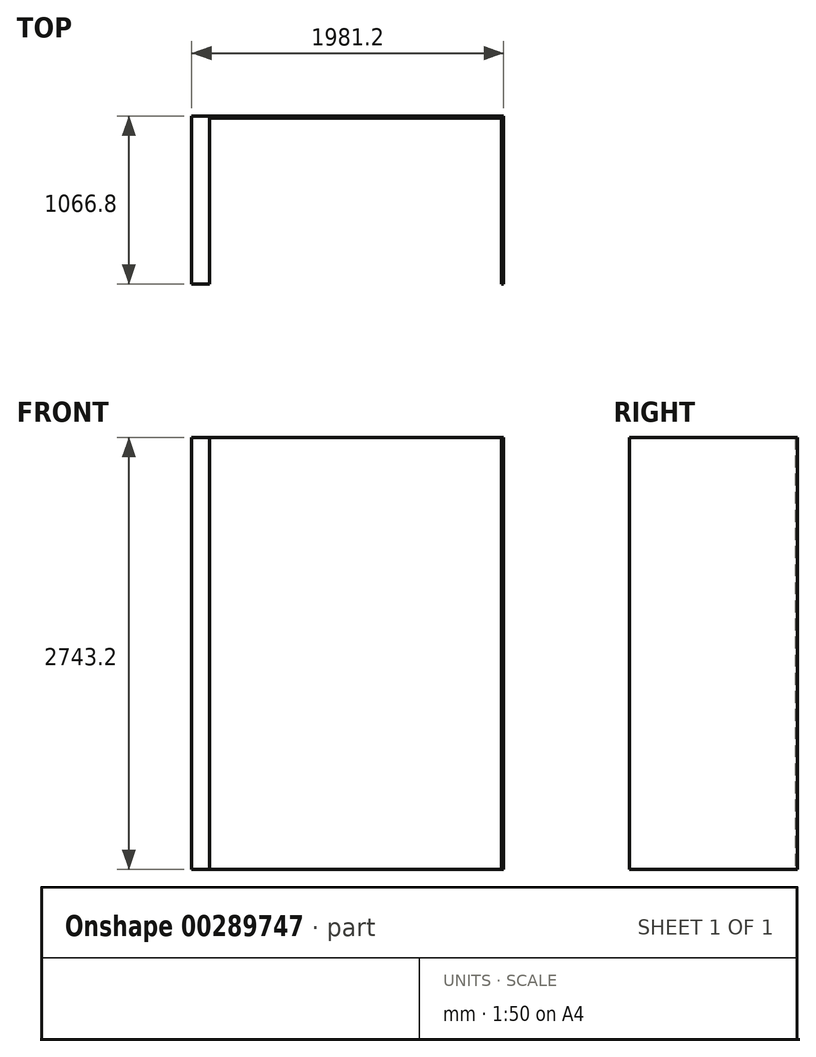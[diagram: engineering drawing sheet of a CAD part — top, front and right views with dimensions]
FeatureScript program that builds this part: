
annotation { "Feature Type Name" : "Feature", "Feature Type Description" : "" }
export const myFeature = defineFeature(function(context is Context, id is Id, definition is map)
    precondition{}
    {
        {
            var Q0;
            Q0=qCreatedBy(makeId("Top.planeOp"),FACE);
            var sketch = newSketch(context, id + "F0", { "sketchPlane" : qUnion([Q0])});
            skLineSegment(sketch, "E0.bottom", {"start": v(990.6, -533.4) * mm, "end": v(-990.6, -533.4) * mm});
            skLineSegment(sketch, "E0.top", {"start": v(990.6, 533.4) * mm, "end": v(-990.6, 533.4) * mm});
            skLineSegment(sketch, "E0.left", {"start": v(990.6, -533.4) * mm, "end": v(990.6, 533.4) * mm});
            skLineSegment(sketch, "E0.right", {"start": v(-990.6, -533.4) * mm, "end": v(-990.6, 533.4) * mm});
            skPoint(sketch, "E0.middle", {"position": v(0, 0) * mm});
            skLineSegment(sketch, "E1", {"start": v(-876.3, -533.4) * mm, "end": v(-876.3, 520.7) * mm});
            skLineSegment(sketch, "E2", {"start": v(-876.3, 520.7) * mm, "end": v(977.9, 520.7) * mm});
            skLineSegment(sketch, "E3", {"start": v(977.9, 520.7) * mm, "end": v(977.9, -533.4) * mm});
            skLineSegment(sketch, "E4", {"start": v(977.9, -533.4) * mm, "end": v(990.6, -533.4) * mm});
            skSolve(sketch);
        }
        {
            var Q0;
            Q0=makeQuery(id+"F0.imprint","IMPRINT",FACE,{"disambiguationData":[TD([[makeQuery(id+"F0.imprint","IMPRINT",EDGE,{"derivedFrom":sQuery(id+"F0.wireOp",EDGE,"E0.top")}),1.0]])]});
            extrude(context, id + "F1", {"entities" : qUnion([Q0]), "depth" : 2743.2 * mm, "offsetDistance" : 30.48 * mm});
        }
    });
